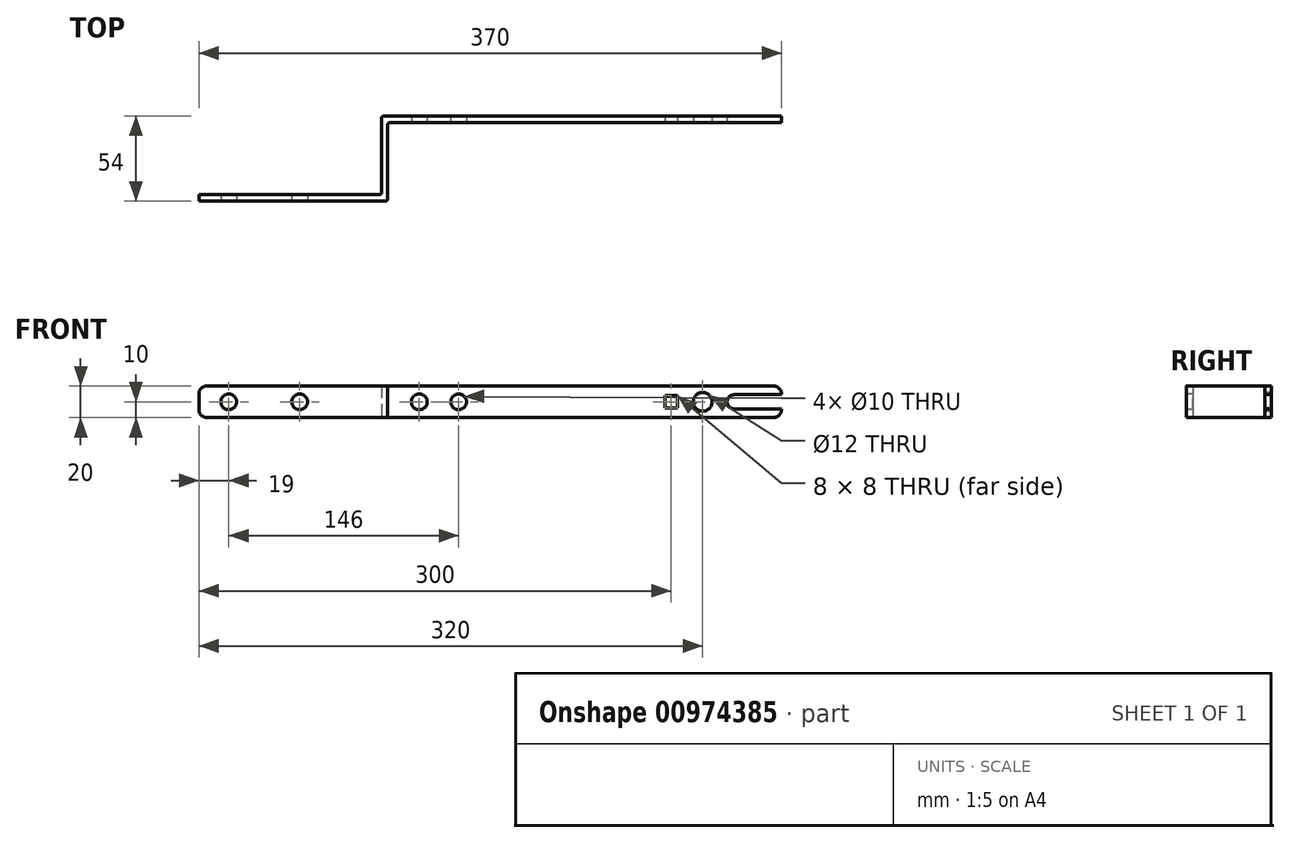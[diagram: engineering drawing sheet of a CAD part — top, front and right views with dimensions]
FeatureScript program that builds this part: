
annotation { "Feature Type Name" : "Feature", "Feature Type Description" : "" }
export const myFeature = defineFeature(function(context is Context, id is Id, definition is map)
    precondition{}
    {
        {
            assignVariable(context, id + "F0", {"name" : "PlatLargeur", "anyValue" : 20});
        }
        {
            var Q0;
            Q0=qCreatedBy(makeId("Top.planeOp"),FACE);
            var sketch = newSketch(context, id + "F1", { "sketchPlane" : qUnion([Q0])});
            skLineSegment(sketch, "E0", {"start": v(0, 50) * mm, "end": v(250, 50) * mm});
            skLineSegment(sketch, "E1", {"start": v(0, 50) * mm, "end": v(0, 0) * mm});
            skLineSegment(sketch, "E2", {"start": v(0, 0) * mm, "end": v(-120, 0) * mm});
            skLineSegment(sketch, "E3", {"start": v(0, 0) * mm, "end": v(225.63, 0) * mm, "construction": true});
            skLineSegment(sketch, "E4.0", {"start": v(-4, 4) * mm, "end": v(-120, 4) * mm});
            skLineSegment(sketch, "E4.1", {"start": v(-4, 54) * mm, "end": v(-4, 4) * mm});
            skLineSegment(sketch, "E4.2", {"start": v(-4, 54) * mm, "end": v(250, 54) * mm});
            skLineSegment(sketch, "E5", {"start": v(250, 54) * mm, "end": v(250, 50) * mm});
            skLineSegment(sketch, "E6", {"start": v(-120, 4) * mm, "end": v(-120, 0) * mm});
            skSolve(sketch);
        }
        {
            var Q0;
            Q0=makeQuery(id+"F1.imprint","IMPRINT",FACE,{"disambiguationData":[TD([[makeQuery(id+"F1.imprint","IMPRINT",EDGE,{"derivedFrom":sQuery(id+"F1.wireOp",EDGE,"E0")}),1.0]])]});
            extrude(context, id + "F2", {"entities" : qUnion([Q0]), "endBound" : BoundingType.SYMMETRIC, "depth" : (getVariable(context, 'PlatLargeur')) * mm, "offsetDistance" : 25 * mm});
        }
        {
            var Q0;
            Q0=qCreatedBy(makeId("Front.planeOp"),FACE);
            var sketch = newSketch(context, id + "F3", { "sketchPlane" : qUnion([Q0])});
            skCircle(sketch, "E7", {"center": v(-101, 0) * mm, "radius": 5 * mm});
            skCircle(sketch, "E8", {"center": v(-56, 0) * mm, "radius": 5 * mm});
            skCircle(sketch, "E9", {"center": v(20, 0) * mm, "radius": 5 * mm});
            skCircle(sketch, "E10", {"center": v(45, 0) * mm, "radius": 5 * mm});
            skCircle(sketch, "E11", {"center": v(200, 0) * mm, "radius": 6 * mm});
            skCircle(sketch, "E12", {"center": v(220, 0) * mm, "radius": 4.5 * mm});
            skLineSegment(sketch, "E13.bottom", {"start": v(176, 4) * mm, "end": v(184, 4) * mm});
            skLineSegment(sketch, "E13.top", {"start": v(176, -4) * mm, "end": v(184, -4) * mm});
            skLineSegment(sketch, "E13.left", {"start": v(176, 4) * mm, "end": v(176, -4) * mm});
            skLineSegment(sketch, "E13.right", {"start": v(184, 4) * mm, "end": v(184, -4) * mm});
            skPoint(sketch, "E13.middle", {"position": v(180, 0) * mm});
            skLineSegment(sketch, "E14", {"start": v(250, 4.5) * mm, "end": v(220, 4.5) * mm});
            skLineSegment(sketch, "E15.MirrorCS", {"start": v(250, -4.5) * mm, "end": v(220, -4.5) * mm});
            skLineSegment(sketch, "E16.0", {"start": v(250, 10) * mm, "end": v(250, -10) * mm});
            skSolve(sketch);
        }
        {
            var Q0;
            Q0 = qSketchRegion(id + "F3", true);
            extrude(context, id + "F4", {"entities" : qUnion([Q0]), "operationType" : NewBodyOperationType.REMOVE, "endBound" : BoundingType.THROUGH_ALL, "oppositeDirection" : true, "depth" : 25 * mm, "offsetDistance" : 25 * mm});
        }
        {
            var Q0;
            Q0=makeQuery(id+"F4.boolean.*.tempSMBoolean.smUpdate.copyWalls","SUBSTITUTION",EDGE,{"derivedFrom":makeQuery(id+"FEZUnEG7UqoA3x5_0.wallThicken","SWEPT_EDGE",EDGE,{"disambiguationData":[ownerDisambiguation([makeQuery(id+"FEZUnEG7UqoA3x5_0.extrude.opExtrude","SWEPT_FACE",FACE,{"disambiguationData":[OSD([sQuery(id+"F1.wireOp",EDGE,"E2")])]})])],"derivedFromVertices":[makeQuery(id+"FEZUnEG7UqoA3x5_0.extrude.opExtrude","CAP_VERTEX",VERTEX,{"disambiguationData":[OSD([sQuery(id+"F1.wireOp",VERTEX,"E2.end")])],"isStart":false})]})});
            var Q1;
            Q1=makeQuery(id+"F4.boolean.*.tempSMBoolean.smUpdate.copyWalls","SUBSTITUTION",EDGE,{"derivedFrom":makeQuery(id+"FEZUnEG7UqoA3x5_0.wallThicken","SWEPT_EDGE",EDGE,{"disambiguationData":[ownerDisambiguation([makeQuery(id+"FEZUnEG7UqoA3x5_0.extrude.opExtrude","SWEPT_FACE",FACE,{"disambiguationData":[OSD([sQuery(id+"F1.wireOp",EDGE,"E2")])]})])],"derivedFromVertices":[makeQuery(id+"FEZUnEG7UqoA3x5_0.extrude.opExtrude","CAP_VERTEX",VERTEX,{"disambiguationData":[OSD([sQuery(id+"F1.wireOp",VERTEX,"E2.end")])],"isStart":true})]})});
            var Q2;
            Q2=makeQuery(id+"F4.boolean.*.tempSMBoolean.smUpdate.copyWalls","SUBSTITUTION",EDGE,{"derivedFrom":makeQuery(id+"FEZUnEG7UqoA3x5_0.wallThicken","SWEPT_EDGE",EDGE,{"disambiguationData":[ownerDisambiguation([makeQuery(id+"FEZUnEG7UqoA3x5_0.extrude.opExtrude","SWEPT_FACE",FACE,{"disambiguationData":[OSD([sQuery(id+"F1.wireOp",EDGE,"E0")])]})])],"derivedFromVertices":[makeQuery(id+"FEZUnEG7UqoA3x5_0.extrude.opExtrude","CAP_VERTEX",VERTEX,{"disambiguationData":[OSD([sQuery(id+"F1.wireOp",VERTEX,"E0.end")])],"isStart":false})]})});
            var Q3;
            Q3=makeQuery(id+"F4.boolean.*.tempSMBoolean.smUpdate.copyWalls","SUBSTITUTION",EDGE,{"derivedFrom":makeQuery(id+"FEZUnEG7UqoA3x5_0.wallThicken","SWEPT_EDGE",EDGE,{"disambiguationData":[ownerDisambiguation([makeQuery(id+"FEZUnEG7UqoA3x5_0.extrude.opExtrude","SWEPT_FACE",FACE,{"disambiguationData":[OSD([sQuery(id+"F1.wireOp",EDGE,"E0")])]})])],"derivedFromVertices":[makeQuery(id+"FEZUnEG7UqoA3x5_0.extrude.opExtrude","CAP_VERTEX",VERTEX,{"disambiguationData":[OSD([sQuery(id+"F1.wireOp",VERTEX,"E0.end")])],"isStart":true})]})});
            var Q4;
            Q4=makeQuery(id+"F2.opExtrude","CAP_EDGE",EDGE,{"disambiguationData":[OSD([sQuery(id+"F1.wireOp",EDGE,"E6")])],"isStart":false});
            var Q5;
            Q5=makeQuery(id+"F2.opExtrude","CAP_EDGE",EDGE,{"disambiguationData":[OSD([sQuery(id+"F1.wireOp",EDGE,"E6")])],"isStart":true});
            var Q6;
            Q6=makeQuery(id+"F2.opExtrude","CAP_EDGE",EDGE,{"disambiguationData":[OSD([sQuery(id+"F1.wireOp",EDGE,"E5")])],"isStart":true});
            var Q7;
            Q7=makeQuery(id+"F2.opExtrude","CAP_EDGE",EDGE,{"disambiguationData":[OSD([sQuery(id+"F1.wireOp",EDGE,"E5")])],"isStart":false});
            fillet(context, id + "F5", {"entities" : qUnion([Q0, Q1, Q2, Q3, Q4, Q5, Q6, Q7]), "radius" : 5 * mm, "tangentPropagation" : true, "allowEdgeOverflow" : false});
        }
        {
            var Q0;
            Q0=makeQuery(id+"F2.opExtrude","SWEPT_EDGE",EDGE,{"disambiguationData":[OSD([sQuery(id+"F1.wireOp",EDGE,"E4.1"),sQuery(id+"F1.wireOp",EDGE,"E4.2")])]});
            var Q1;
            Q1=makeQuery(id+"F2.opExtrude","SWEPT_EDGE",EDGE,{"disambiguationData":[OSD([sQuery(id+"F1.wireOp",EDGE,"E0"),sQuery(id+"F1.wireOp",EDGE,"E1")])]});
            var Q2;
            Q2=makeQuery(id+"F2.opExtrude","SWEPT_EDGE",EDGE,{"disambiguationData":[OSD([sQuery(id+"F1.wireOp",EDGE,"E1"),sQuery(id+"F1.wireOp",EDGE,"E2")])]});
            var Q3;
            Q3=makeQuery(id+"F2.opExtrude","SWEPT_EDGE",EDGE,{"disambiguationData":[OSD([sQuery(id+"F1.wireOp",EDGE,"E4.0"),sQuery(id+"F1.wireOp",EDGE,"E4.1")])]});
            fillet(context, id + "F6", {"entities" : qUnion([Q0, Q1, Q2, Q3]), "radius" : 1.5 * mm, "tangentPropagation" : true, "allowEdgeOverflow" : false});
        }
    });
